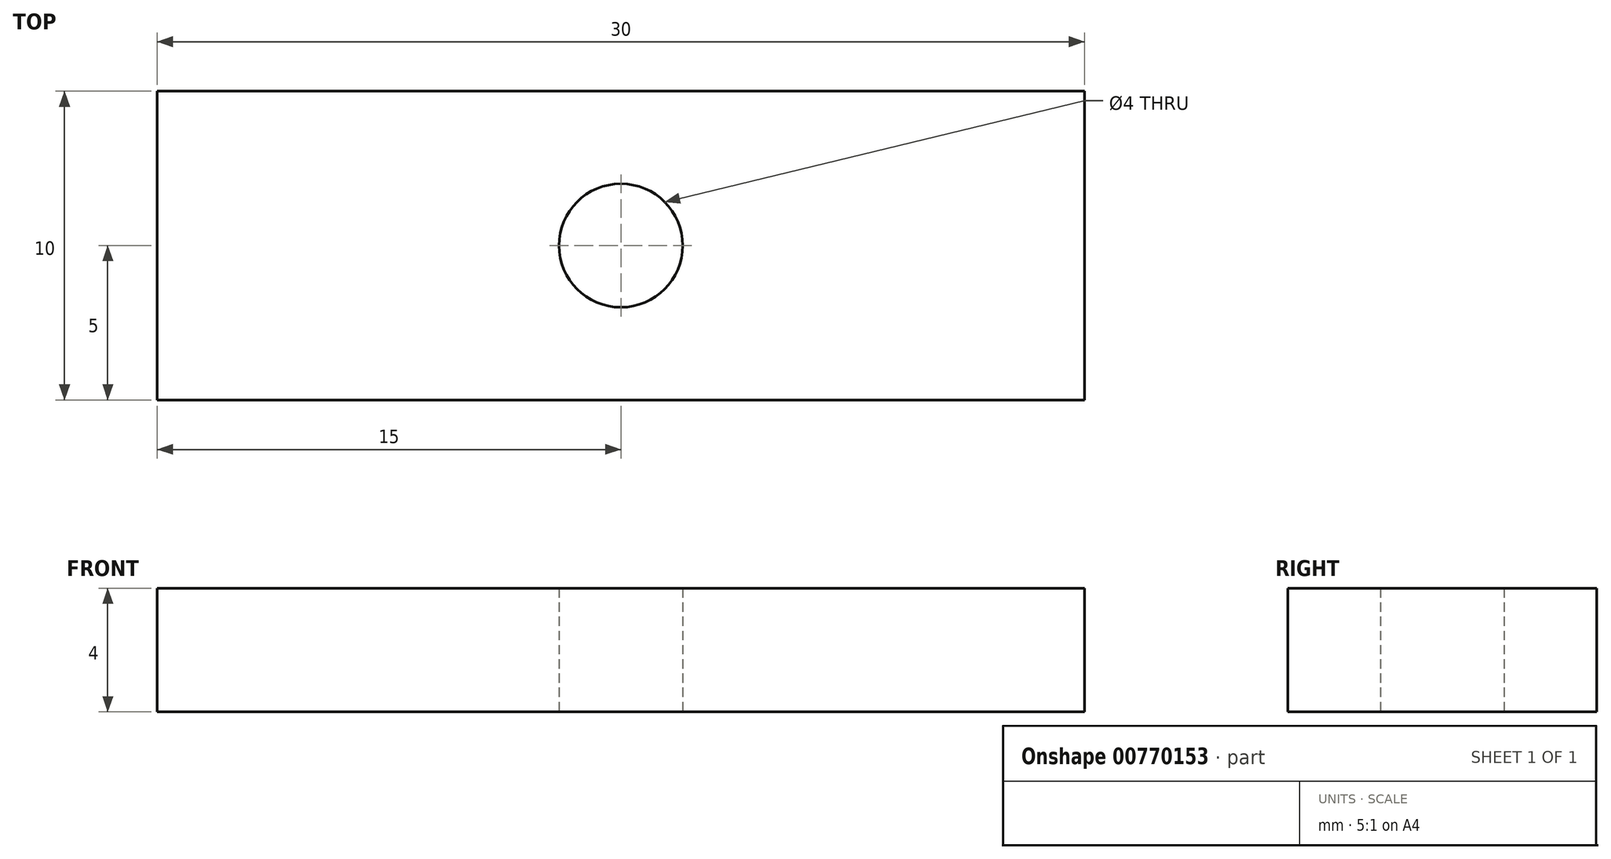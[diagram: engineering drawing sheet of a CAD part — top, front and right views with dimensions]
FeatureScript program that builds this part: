
annotation { "Feature Type Name" : "Feature", "Feature Type Description" : "" }
export const myFeature = defineFeature(function(context is Context, id is Id, definition is map)
    precondition{}
    {
        {
            var Q0;
            Q0=qCreatedBy(makeId("Top.planeOp"),FACE);
            var sketch = newSketch(context, id + "F0", { "sketchPlane" : qUnion([Q0])});
            skLineSegment(sketch, "E0.bottom", {"start": v(-15, 5) * mm, "end": v(15, 5) * mm});
            skLineSegment(sketch, "E0.top", {"start": v(-15, -5) * mm, "end": v(15, -5) * mm});
            skLineSegment(sketch, "E0.left", {"start": v(-15, 5) * mm, "end": v(-15, -5) * mm});
            skLineSegment(sketch, "E0.right", {"start": v(15, 5) * mm, "end": v(15, -5) * mm});
            skPoint(sketch, "E0.middle", {"position": v(0, 0) * mm});
            skCircle(sketch, "E1", {"center": v(0, 0) * mm, "radius": 2 * mm});
            skSolve(sketch);
        }
        {
            var Q0;
            Q0=qSketchRegion(id+"F0",true);
            extrude(context, id + "F1", {"entities" : qUnion([Q0]), "depth" : 4 * mm, "offsetDistance" : 25 * mm});
        }
    });
